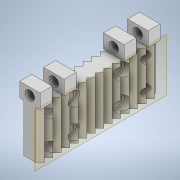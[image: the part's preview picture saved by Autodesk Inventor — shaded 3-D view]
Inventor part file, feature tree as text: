
AUTODESK INVENTOR PART (.ipt)
format: ipt  version: 2020 (Build 240168000, 168)  size: 372,736 bytes
history: native  units: in
note: dims shown in document units (in); Inventor stores cm internally (conversion verified against a paired STEP export)
features: extrude x7, sketch x7, mirror x3, plane x1
ambient origin geometry x8: Origin, YZ Plane, XZ Plane, XY Plane, X Axis, Y Axis, Z Axis, Center Point
bodies: Solid1 (feature_tree)
feature tree (18):
  extrude  "Extrusion1"  Depth=1.9685in
  extrude  "Extrusion2"  Depth=0.0984in
  mirror  "Mirror1"
  extrude  "Extrusion3"  Depth=0.7874in TaperAngle=0.0deg
  plane  "Work Plane1"
  extrude  "Extrusion4"  Depth=0.1575in
  mirror  "Mirror2"
  extrude  "Extrusion5"  Depth=0.1575in
  extrude  "Extrusion6"  Depth=1.1811in
  mirror  "Mirror3"
  extrude  "Extrusion7"  Depth=0.2362in
  sketch  "Sketch1"  dims[d0=0.1969in d1=1.9685in]
  sketch  "Sketch2"  dims[d2=0.7874in d3=0.0in d4=0.0984in]
  sketch  "Sketch3"  dims[d5=45.0deg d6=0.7874in d7=0.0in]
  sketch  "Sketch4"  dims[d8=0.1575in d9=0.1575in]
  sketch  "Sketch5"  dims[d10=0.1575in d11=0.1575in]
  sketch  "Sketch6"  dims[d12=1.1811in d13=0.0in d14=0.1732in]
  sketch  "Sketch7"  dims[d15=0.2362in d16=0.2362in d17=0.2362in d18=0.2362in d19=0.1181in d20=0.0in d21=0.1575in d22=0.1575in d23=0.1575in d24=0.1575in d25=0.7874in d26=0.0in d27=0.3361in d28=0.1969in d29=0.3361in d30=0.1969in d31=0.2362in d32=0.0in d33=0.1575in d34=1.9685in d35=0.0in]
